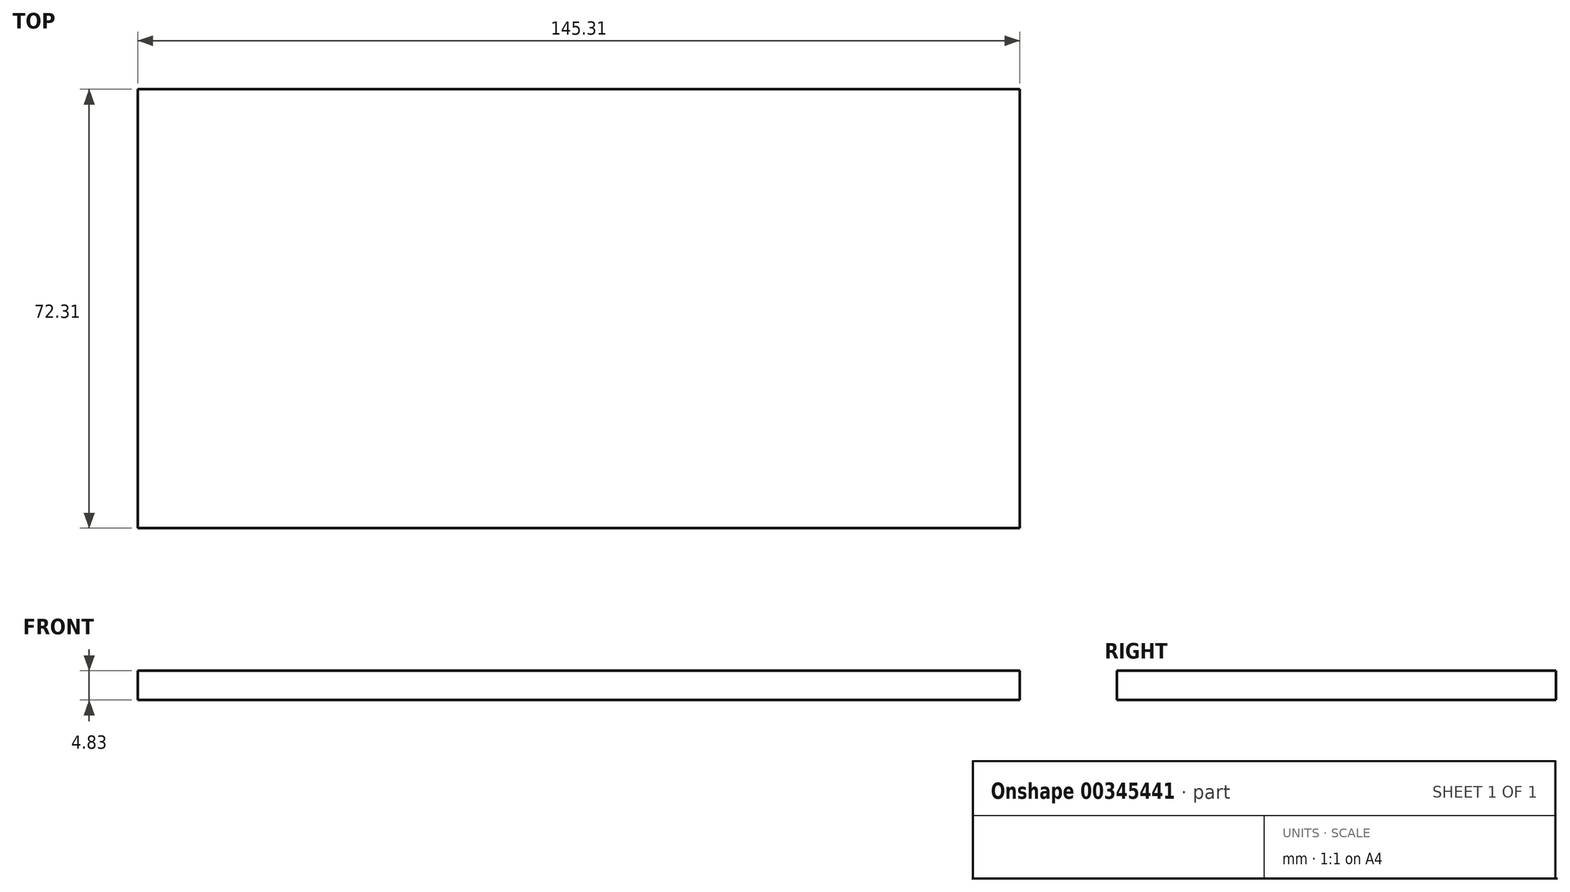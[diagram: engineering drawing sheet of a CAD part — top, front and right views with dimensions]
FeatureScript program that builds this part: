
annotation { "Feature Type Name" : "Feature", "Feature Type Description" : "" }
export const myFeature = defineFeature(function(context is Context, id is Id, definition is map)
    precondition{}
    {
        {
            var Q0;
            Q0=qCreatedBy(makeId("Top.planeOp"),FACE);
            var sketch = newSketch(context, id + "F0", { "sketchPlane" : qUnion([Q0])});
            skLineSegment(sketch, "E0.bottom", {"start": v(-79.8, -53.84) * mm, "end": v(65.5, -53.84) * mm});
            skLineSegment(sketch, "E0.top", {"start": v(-79.8, 18.47) * mm, "end": v(65.5, 18.47) * mm});
            skLineSegment(sketch, "E0.left", {"start": v(-79.8, -53.84) * mm, "end": v(-79.8, 18.47) * mm});
            skLineSegment(sketch, "E0.right", {"start": v(65.5, -53.84) * mm, "end": v(65.5, 18.47) * mm});
            skSolve(sketch);
        }
        {
            var Q0;
            Q0=makeQuery(id+"F0.imprint","IMPRINT",FACE,{"disambiguationData":[TD([[makeQuery(id+"F0.imprint","IMPRINT",EDGE,{"derivedFrom":sQuery(id+"F0.wireOp",EDGE,"E0.bottom")}),1.0]])]});
            extrude(context, id + "F1", {"entities" : qUnion([Q0]), "depth" : 4.83 * mm});
        }
    });
